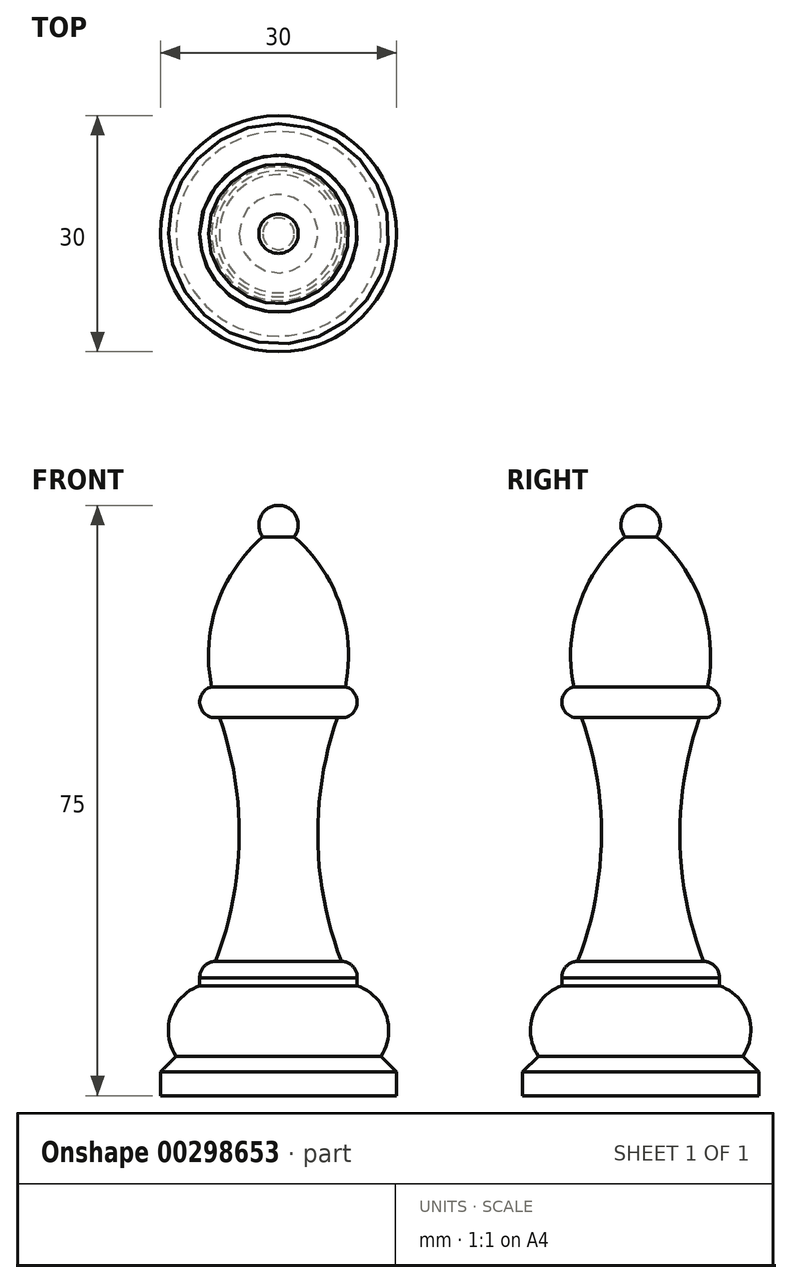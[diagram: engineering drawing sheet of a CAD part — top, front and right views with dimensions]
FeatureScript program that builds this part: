
annotation { "Feature Type Name" : "Feature", "Feature Type Description" : "" }
export const myFeature = defineFeature(function(context is Context, id is Id, definition is map)
    precondition{}
    {
        {
            var Q0;
            Q0=qCreatedBy(makeId("Front.planeOp"),FACE);
            var sketch = newSketch(context, id + "F0", { "sketchPlane" : qUnion([Q0])});
            skArc(sketch, "E0", {"start": v(2, -4) * mm, "mid": v(2.24, -1.38) * mm, "end": v(0, 0) * mm});
            skArc(sketch, "E1", {"start": v(8.5, -23.06) * mm, "mid": v(7.82, -12.65) * mm, "end": v(2, -4) * mm});
            skArc(sketch, "E2", {"start": v(8.5, -26.93) * mm, "mid": v(10, -25) * mm, "end": v(8.5, -23.06) * mm});
            skLineSegment(sketch, "E3", {"start": v(8.5, -26.93) * mm, "end": v(7.5, -26.93) * mm});
            skArc(sketch, "E4", {"start": v(7.5, -26.93) * mm, "mid": v(5, -42.49) * mm, "end": v(8, -57.95) * mm});
            skArc(sketch, "E5", {"start": v(10, -60.03) * mm, "mid": v(9.44, -58.57) * mm, "end": v(8, -57.95) * mm});
            skLineSegment(sketch, "E6", {"start": v(10, -60.03) * mm, "end": v(10, -61.03) * mm});
            skArc(sketch, "E7", {"start": v(13, -70) * mm, "mid": v(13.69, -64.78) * mm, "end": v(10, -61.03) * mm});
            skLineSegment(sketch, "E8", {"start": v(13, -70) * mm, "end": v(15, -72) * mm});
            skLineSegment(sketch, "E9", {"start": v(15, -72) * mm, "end": v(15, -75) * mm});
            skLineSegment(sketch, "E10", {"start": v(15, -75) * mm, "end": v(0, -75) * mm});
            skLineSegment(sketch, "E11", {"start": v(0, -75) * mm, "end": v(0, 0) * mm});
            skSolve(sketch);
        }
        {
            var Q0;
            Q0 = qSketchRegion(id + "F0", true);
            var Q1;
            Q1=sQuery(id+"F0.wireOp",EDGE,"E11");
            revolve(context, id + "F1", {"entities" : qUnion([Q0]), "axis" : qUnion([Q1]), "revolveType" : RevolveType.FULL});
        }
    });
